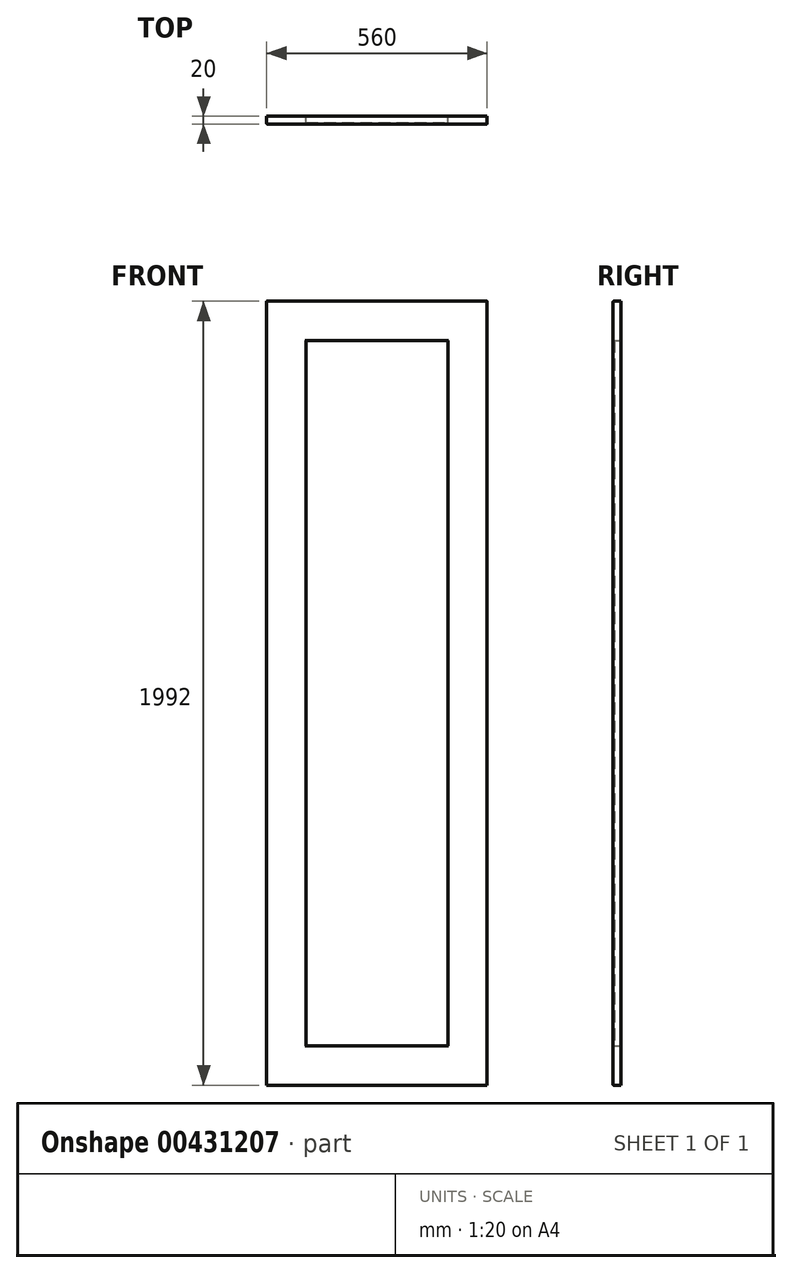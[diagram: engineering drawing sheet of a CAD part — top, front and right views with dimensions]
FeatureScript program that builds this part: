
annotation { "Feature Type Name" : "Feature", "Feature Type Description" : "" }
export const myFeature = defineFeature(function(context is Context, id is Id, definition is map)
    precondition{}
    {
        {
            var Q0;
            Q0=qCreatedBy(makeId("Front.planeOp"),FACE);
            var sketch = newSketch(context, id + "F0", { "sketchPlane" : qUnion([Q0])});
            skLineSegment(sketch, "E0.bottom", {"start": v(0, 0) * mm, "end": v(100, 0) * mm});
            skLineSegment(sketch, "E0.top", {"start": v(0, 1992) * mm, "end": v(100, 1992) * mm});
            skLineSegment(sketch, "E0.left", {"start": v(0, 0) * mm, "end": v(0, 1992) * mm});
            skLineSegment(sketch, "E0.right", {"start": v(100, 0) * mm, "end": v(100, 1992) * mm});
            skLineSegment(sketch, "E1.bottom", {"start": v(-360, 1992) * mm, "end": v(-460, 1992) * mm});
            skLineSegment(sketch, "E1.top", {"start": v(-360, 0) * mm, "end": v(-460, 0) * mm});
            skLineSegment(sketch, "E1.left", {"start": v(-360, 1992) * mm, "end": v(-360, 0) * mm});
            skLineSegment(sketch, "E1.right", {"start": v(-460, 1992) * mm, "end": v(-460, 0) * mm});
            skLineSegment(sketch, "E2.bottom", {"start": v(-360, 1992) * mm, "end": v(0, 1992) * mm});
            skLineSegment(sketch, "E2.top", {"start": v(-360, 1892) * mm, "end": v(0, 1892) * mm});
            skLineSegment(sketch, "E2.left", {"start": v(-360, 1992) * mm, "end": v(-360, 1892) * mm});
            skLineSegment(sketch, "E2.right", {"start": v(0, 1992) * mm, "end": v(0, 1892) * mm});
            skLineSegment(sketch, "E3.bottom", {"start": v(-360, 0) * mm, "end": v(0, 0) * mm});
            skLineSegment(sketch, "E3.top", {"start": v(-360, 100) * mm, "end": v(0, 100) * mm});
            skLineSegment(sketch, "E3.left", {"start": v(-360, 0) * mm, "end": v(-360, 100) * mm});
            skLineSegment(sketch, "E3.right", {"start": v(0, 0) * mm, "end": v(0, 100) * mm});
            skSolve(sketch);
        }
        {
            var Q0;
            Q0=makeQuery(id+"F0.imprint","IMPRINT",FACE,{"disambiguationData":[TD([[makeQuery(id+"F0.imprint","IMPRINT",EDGE,{"derivedFrom":sQuery(id+"F0.wireOp",EDGE,"E1.bottom")}),1.0]])]});
            var Q1;
            Q1=makeQuery(id+"F0.imprint","IMPRINT",FACE,{"disambiguationData":[TD([[makeQuery(id+"F0.imprint","IMPRINT",EDGE,{"derivedFrom":sQuery(id+"F0.wireOp",EDGE,"E3.bottom")}),1.0]])]});
            var Q2;
            Q2=makeQuery(id+"F0.imprint","IMPRINT",FACE,{"disambiguationData":[TD([[makeQuery(id+"F0.imprint","IMPRINT",EDGE,{"derivedFrom":sQuery(id+"F0.wireOp",EDGE,"E2.bottom")}),-1.0]])]});
            var Q3;
            Q3=makeQuery(id+"F0.imprint","IMPRINT",FACE,{"disambiguationData":[TD([[makeQuery(id+"F0.imprint","IMPRINT",EDGE,{"derivedFrom":sQuery(id+"F0.wireOp",EDGE,"E0.bottom")}),1.0]])]});
            extrude(context, id + "F1", {"entities" : qUnion([Q0, Q1, Q2, Q3]), "depth" : 20 * mm});
        }
        {
            var Q0;
            Q0=makeQuery(id+"F1.opExtrude","CAP_EDGE",EDGE,{"disambiguationData":[OSD([sQuery(id+"F0.wireOp",EDGE,"E1.right")])],"isStart":false});
            var Q1;
            Q1=makeQuery(id+"F1.opExtrude","CAP_EDGE",EDGE,{"disambiguationData":[OSD([sQuery(id+"F0.wireOp",EDGE,"E1.top")])],"isStart":false});
            var Q2;
            Q2=makeQuery(id+"F1.opExtrude","CAP_EDGE",EDGE,{"disambiguationData":[OSD([sQuery(id+"F0.wireOp",EDGE,"E0.bottom")])],"isStart":false});
            var Q3;
            Q3=makeQuery(id+"F1.opExtrude","CAP_EDGE",EDGE,{"disambiguationData":[OSD([sQuery(id+"F0.wireOp",EDGE,"E0.right")])],"isStart":false});
            var Q4;
            Q4=makeQuery(id+"F1.opExtrude","CAP_EDGE",EDGE,{"disambiguationData":[OSD([sQuery(id+"F0.wireOp",EDGE,"E0.top")])],"isStart":false});
            var Q5;
            Q5=makeQuery(id+"F1.opExtrude","CAP_EDGE",EDGE,{"disambiguationData":[OSD([sQuery(id+"F0.wireOp",EDGE,"E1.bottom")])],"isStart":false});
            var Q6;
            Q6=makeQuery(id+"F1.opExtrude","CAP_EDGE",EDGE,{"disambiguationData":[OSD([sQuery(id+"F0.wireOp",EDGE,"E1.left"),sQuery(id+"F0.wireOp",EDGE,"E2.left"),sQuery(id+"F0.wireOp",EDGE,"E3.left")])],"isStart":false});
            var Q7;
            Q7=makeQuery(id+"F1.opExtrude","CAP_EDGE",EDGE,{"disambiguationData":[OSD([sQuery(id+"F0.wireOp",EDGE,"E0.left"),sQuery(id+"F0.wireOp",EDGE,"E2.right"),sQuery(id+"F0.wireOp",EDGE,"E3.right")])],"isStart":false});
            fillet(context, id + "F2", {"entities" : qUnion([Q0, Q1, Q2, Q3, Q4, Q5, Q6, Q7]), "radius" : 2 * mm, "tangentPropagation" : true, "allowEdgeOverflow" : false});
        }
        {
            var Q0;
            Q0=makeQuery(id+"F1.opExtrude","CAP_FACE",FACE,{"disambiguationData":[OSD([sQuery(id+"F0.wireOp",EDGE,"E0.bottom"),sQuery(id+"F0.wireOp",EDGE,"E0.top"),sQuery(id+"F0.wireOp",EDGE,"E0.left"),sQuery(id+"F0.wireOp",EDGE,"E0.right"),sQuery(id+"F0.wireOp",EDGE,"E1.bottom"),sQuery(id+"F0.wireOp",EDGE,"E1.top"),sQuery(id+"F0.wireOp",EDGE,"E1.left"),sQuery(id+"F0.wireOp",EDGE,"E1.right"),sQuery(id+"F0.wireOp",EDGE,"E2.bottom"),sQuery(id+"F0.wireOp",EDGE,"E2.top"),sQuery(id+"F0.wireOp",EDGE,"E3.bottom"),sQuery(id+"F0.wireOp",EDGE,"E3.top")])],"isStart":true});
            var sketch = newSketch(context, id + "F3", { "sketchPlane" : qUnion([Q0])});
            skLineSegment(sketch, "E4.0", {"start": v(-98, 1990) * mm, "end": v(458, 1990) * mm});
            skLineSegment(sketch, "E4.1", {"start": v(458, 1990) * mm, "end": v(458, 2) * mm});
            skLineSegment(sketch, "E4.2", {"start": v(-100, 1992) * mm, "end": v(-100, 0) * mm});
            skLineSegment(sketch, "E4.3", {"start": v(-100, 0) * mm, "end": v(460, 0) * mm});
            skSolve(sketch);
        }
        {
            var Q0;
            Q0=makeQuery(id+"F3.imprint","IMPRINT",FACE,{"disambiguationData":[TD([[makeQuery(id+"F3.imprint","IMPRINT",EDGE,{"derivedFrom":makeQuery(id+"F1.opExtrude","CAP_EDGE",EDGE,{"disambiguationData":[OSD([sQuery(id+"F0.wireOp",EDGE,"E0.left")])],"isStart":true})}),-1.0]])]});
            extrude(context, id + "F4", {"entities" : qUnion([Q0]), "oppositeDirection" : true, "depth" : 16 * mm});
        }
    });
